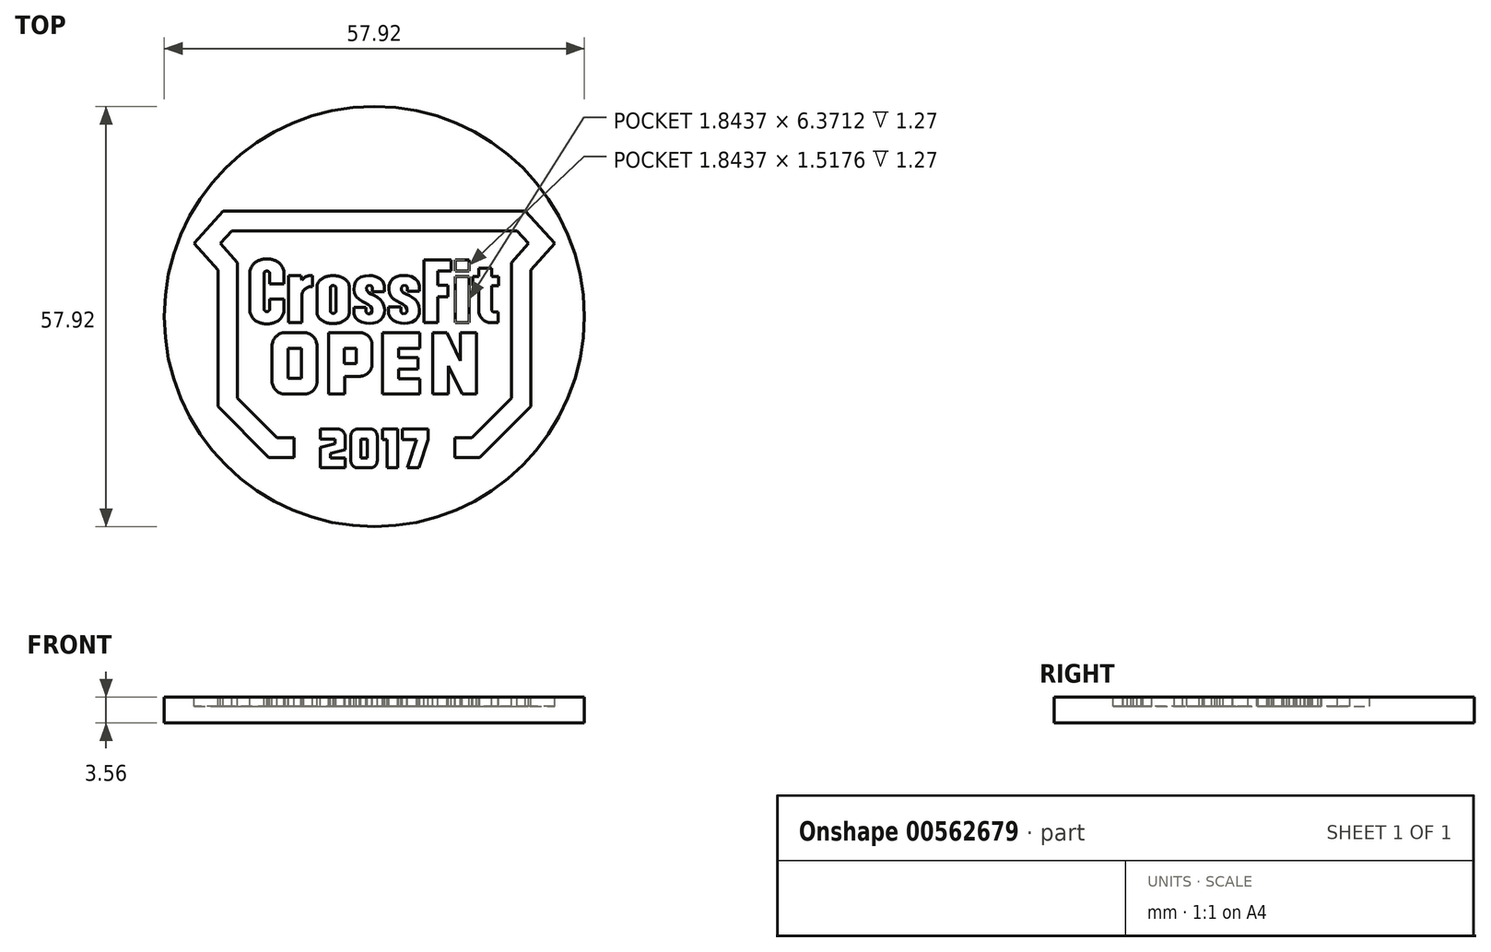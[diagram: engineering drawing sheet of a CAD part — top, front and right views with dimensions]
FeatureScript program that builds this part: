
annotation { "Feature Type Name" : "Feature", "Feature Type Description" : "" }
export const myFeature = defineFeature(function(context is Context, id is Id, definition is map)
    precondition{}
    {
        {
            var Q0;
            Q0=qCreatedBy(makeId("Top.planeOp"),FACE);
            var sketch = newSketch(context, id + "F0", { "sketchPlane" : qUnion([Q0])});
            skCircle(sketch, "E0", {"center": v(0, 0) * mm, "radius": 28.96 * mm});
            skSolve(sketch);
        }
        {
            var Q0;
            Q0=makeQuery(id+"F0.imprint","IMPRINT",FACE,{"disambiguationData":[TD([[makeQuery(id+"F0.imprint","IMPRINT",EDGE,{"derivedFrom":sQuery(id+"F0.wireOp",EDGE,"E0")}),1.0]])]});
            extrude(context, id + "F1", {"entities" : qUnion([Q0]), "depth" : 3.56 * mm, "offsetDistance" : 25.4 * mm});
        }
        {
            var Q0;
            Q0=makeQuery(id+"F1.opExtrude","CAP_FACE",FACE,{"disambiguationData":[OSD([sQuery(id+"F0.wireOp",EDGE,"E0")])],"isStart":false});
            var sketch = newSketch(context, id + "F2", { "sketchPlane" : qUnion([Q0])});
            skPoint(sketch, "E1", {"position": v(0.13, -0.67) * mm});
            skLineSegment(sketch, "E2", {"start": v(-15.2, 14.53) * mm, "end": v(-15.2, 11.82) * mm});
            skLineSegment(sketch, "E3", {"start": v(-15.2, 11.82) * mm, "end": v(-19.67, 11.82) * mm});
            skLineSegment(sketch, "E4", {"start": v(-19.67, 11.82) * mm, "end": v(-21.25, 10.06) * mm});
            skLineSegment(sketch, "E5", {"start": v(-21.25, 10.06) * mm, "end": v(-18.9, 7.43) * mm});
            skLineSegment(sketch, "E6", {"start": v(-18.9, 7.43) * mm, "end": v(-18.9, -11.25) * mm});
            skLineSegment(sketch, "E7", {"start": v(-18.9, -11.25) * mm, "end": v(-13.44, -16.74) * mm});
            skLineSegment(sketch, "E8", {"start": v(-13.44, -16.74) * mm, "end": v(-11.07, -16.74) * mm});
            skLineSegment(sketch, "E9", {"start": v(-11.07, -16.74) * mm, "end": v(-11.07, -19.45) * mm});
            skLineSegment(sketch, "E10", {"start": v(-11.07, -19.45) * mm, "end": v(-14.54, -19.45) * mm});
            skLineSegment(sketch, "E11", {"start": v(-14.54, -19.45) * mm, "end": v(-21.55, -12.4) * mm});
            skLineSegment(sketch, "E12", {"start": v(-21.55, -12.4) * mm, "end": v(-21.55, 6.37) * mm});
            skLineSegment(sketch, "E13", {"start": v(-21.55, 6.37) * mm, "end": v(-24.85, 10.06) * mm});
            skLineSegment(sketch, "E14", {"start": v(-24.85, 10.06) * mm, "end": v(-20.84, 14.53) * mm});
            skLineSegment(sketch, "E15", {"start": v(-20.84, 14.53) * mm, "end": v(-15.2, 14.53) * mm});
            skLineSegment(sketch, "E16", {"start": v(-14.42, 6) * mm, "end": v(-14.42, 4.47) * mm});
            skLineSegment(sketch, "E17", {"start": v(-14.42, 4.47) * mm, "end": v(-12.48, 4.47) * mm});
            skLineSegment(sketch, "E18", {"start": v(-12.48, 4.47) * mm, "end": v(-12.48, 6.3) * mm});
            skLineSegment(sketch, "E19", {"start": v(-17.15, 6.3) * mm, "end": v(-17.15, 0.62) * mm});
            skLineSegment(sketch, "E20", {"start": v(-14.42, 1) * mm, "end": v(-14.42, 2.43) * mm});
            skLineSegment(sketch, "E21", {"start": v(-14.42, 2.43) * mm, "end": v(-12.48, 2.43) * mm});
            skLineSegment(sketch, "E22", {"start": v(-12.48, 2.43) * mm, "end": v(-12.48, 0.62) * mm});
            skLineSegment(sketch, "E23", {"start": v(-15.2, 6) * mm, "end": v(-15.2, 1) * mm});
            skArc(sketch, "E24", {"start": v(-14.42, 6) * mm, "mid": v(-14.81, 6.27) * mm, "end": v(-15.2, 6) * mm});
            skArc(sketch, "E25", {"start": v(-15.2, 1) * mm, "mid": v(-14.81, 0.68) * mm, "end": v(-14.42, 1) * mm});
            skLineSegment(sketch, "E26", {"start": v(-9.97, 5) * mm, "end": v(-10.1, 5.63) * mm});
            skLineSegment(sketch, "E27", {"start": v(-10.1, 5.63) * mm, "end": v(-11.83, 5.63) * mm});
            skLineSegment(sketch, "E28", {"start": v(-11.83, 5.63) * mm, "end": v(-11.83, -0.85) * mm});
            skLineSegment(sketch, "E29", {"start": v(-11.83, -0.85) * mm, "end": v(-9.98, -0.85) * mm});
            skLineSegment(sketch, "E30", {"start": v(-9.98, -0.85) * mm, "end": v(-9.98, 3.1) * mm});
            skLineSegment(sketch, "E31", {"start": v(-8.5, 5.65) * mm, "end": v(-8.5, 4.11) * mm});
            skArc(sketch, "E32", {"start": v(-8.5, 5.65) * mm, "mid": v(-9.32, 5.53) * mm, "end": v(-9.97, 5) * mm});
            skArc(sketch, "E33", {"start": v(-8.5, 4.11) * mm, "mid": v(-9.44, 3.9) * mm, "end": v(-9.98, 3.1) * mm});
            skLineSegment(sketch, "E34", {"start": v(-7.89, 4.2) * mm, "end": v(-7.89, 0.46) * mm});
            skLineSegment(sketch, "E35", {"start": v(-3.47, 4.2) * mm, "end": v(-3.47, 0.46) * mm});
            skLineSegment(sketch, "E36", {"start": v(-6.05, 4.04) * mm, "end": v(-6.05, 0.68) * mm});
            skLineSegment(sketch, "E37", {"start": v(-5.3, 0.68) * mm, "end": v(-5.3, 4.04) * mm});
            skArc(sketch, "E38", {"start": v(-5.3, 4.04) * mm, "mid": v(-5.68, 4.28) * mm, "end": v(-6.05, 4.04) * mm});
            skArc(sketch, "E39", {"start": v(-6.05, 0.68) * mm, "mid": v(-5.68, 0.43) * mm, "end": v(-5.3, 0.68) * mm});
            skLineSegment(sketch, "E40", {"start": v(-5.68, 3.86) * mm, "end": v(-5.68, 0.84) * mm, "construction": true});
            skLineSegment(sketch, "E41", {"start": v(-7.89, 2.33) * mm, "end": v(-3.47, 2.33) * mm, "construction": true});
            skFitSpline(sketch, "E42.MirrorCS", {"points": [v(-3.47, 4.2) * mm, v(-3.93, 5.06) * mm, v(-4.62, 5.46) * mm, v(-5.68, 5.64) * mm], "startDerivative": vector(-0.46, 3.85) * mm, "endDerivative": vector(-4.22, 0.16) * mm});
            skFitSpline(sketch, "E43.MirrorCS", {"points": [v(-7.89, 0.46) * mm, v(-7.42, -0.4) * mm, v(-6.74, -0.8) * mm, v(-5.68, -0.98) * mm], "startDerivative": vector(0.46, -3.85) * mm, "endDerivative": vector(4.22, -0.16) * mm});
            skFitSpline(sketch, "E44.MirrorCS", {"points": [v(-3.47, 0.46) * mm, v(-3.93, -0.4) * mm, v(-4.62, -0.8) * mm, v(-5.68, -0.98) * mm], "startDerivative": vector(-0.46, -3.85) * mm, "endDerivative": vector(-4.22, -0.16) * mm});
            skFitSpline(sketch, "E45", {"points": [v(-17.15, 6.3) * mm, v(-16.64, 7.26) * mm, v(-16, 7.69) * mm, v(-14.81, 7.96) * mm], "startDerivative": vector(0.97, 4.15) * mm, "endDerivative": vector(4.22, 0.16) * mm});
            skLineSegment(sketch, "E46", {"start": v(-14.81, 5.84) * mm, "end": v(-14.81, 1.08) * mm, "construction": true});
            skFitSpline(sketch, "E47.MirrorCS", {"points": [v(-12.48, 6.3) * mm, v(-12.99, 7.26) * mm, v(-13.62, 7.69) * mm, v(-14.81, 7.96) * mm], "startDerivative": vector(-0.97, 4.15) * mm, "endDerivative": vector(-4.22, 0.16) * mm});
            skLineSegment(sketch, "E48", {"start": v(-17.15, 3.46) * mm, "end": v(-14.81, 3.46) * mm, "construction": true});
            skFitSpline(sketch, "E49.MirrorCS", {"points": [v(-17.15, 0.62) * mm, v(-16.64, -0.34) * mm, v(-16, -0.77) * mm, v(-14.81, -1.04) * mm], "startDerivative": vector(0.97, -4.15) * mm, "endDerivative": vector(4.22, -0.16) * mm});
            skFitSpline(sketch, "E50.MirrorCS", {"points": [v(-12.48, 0.62) * mm, v(-12.99, -0.34) * mm, v(-13.62, -0.77) * mm, v(-14.81, -1.04) * mm], "startDerivative": vector(-0.97, -4.15) * mm, "endDerivative": vector(-4.22, -0.16) * mm});
            skFitSpline(sketch, "E51.MirrorCS", {"points": [v(-7.89, 4.2) * mm, v(-7.42, 5.06) * mm, v(-6.74, 5.46) * mm, v(-5.68, 5.64) * mm], "startDerivative": vector(0.46, 3.85) * mm, "endDerivative": vector(4.22, 0.16) * mm});
            skLineSegment(sketch, "E52", {"start": v(-0.27, 4.07) * mm, "end": v(-0.27, 3.44) * mm});
            skLineSegment(sketch, "E53", {"start": v(-0.27, 3.44) * mm, "end": v(1.39, 3.44) * mm});
            skLineSegment(sketch, "E54", {"start": v(1.39, 3.44) * mm, "end": v(1.39, 4.25) * mm});
            skFitSpline(sketch, "E55", {"points": [v(1.39, 4.25) * mm, v(1.25, 4.73) * mm, v(0.96, 5.08) * mm, v(0.56, 5.36) * mm, v(0, 5.56) * mm, v(-0.4, 5.63) * mm, v(-0.7, 5.64) * mm, v(-1.07, 5.62) * mm, v(-1.62, 5.53) * mm, v(-2.03, 5.35) * mm, v(-2.4, 5.07) * mm, v(-2.62, 4.73) * mm, v(-2.76, 4.31) * mm, v(-2.8, 3.96) * mm, v(-2.78, 3.56) * mm, v(-2.7, 3.15) * mm, v(-2.47, 2.72) * mm, v(-2.25, 2.47) * mm, v(-1.97, 2.27) * mm, v(-1.61, 2.07) * mm, v(-1.3, 1.9) * mm, v(-1.02, 1.76) * mm, v(-0.75, 1.6) * mm, v(-0.5, 1.4) * mm, v(-0.41, 1.28) * mm, v(-0.32, 1.08) * mm, v(-0.3, 0.79) * mm, v(-0.34, 0.57) * mm, v(-0.46, 0.43) * mm, v(-0.64, 0.38) * mm, v(-0.84, 0.39) * mm, v(-1.03, 0.44) * mm, v(-1.16, 0.63) * mm], "startDerivative": vector(-2.14, 14.98) * mm, "endDerivative": vector(-3.94, 13.1) * mm});
            skLineSegment(sketch, "E56", {"start": v(-2.83, 0.39) * mm, "end": v(-2.83, 1.28) * mm});
            skLineSegment(sketch, "E57", {"start": v(-2.83, 1.28) * mm, "end": v(-1.16, 1.28) * mm});
            skLineSegment(sketch, "E58", {"start": v(-1.16, 1.28) * mm, "end": v(-1.16, 0.63) * mm});
            skFitSpline(sketch, "E59", {"points": [v(-2.83, 0.39) * mm, v(-2.67, -0.07) * mm, v(-2.35, -0.45) * mm, v(-1.98, -0.69) * mm, v(-1.5, -0.86) * mm, v(-1.03, -0.94) * mm, v(-0.7, -0.95) * mm, v(-0.34, -0.94) * mm, v(0.21, -0.84) * mm, v(0.6, -0.67) * mm, v(0.97, -0.39) * mm, v(1.22, -0.06) * mm, v(1.37, 0.3) * mm, v(1.42, 0.75) * mm, v(1.4, 1.11) * mm, v(1.3, 1.54) * mm, v(1.1, 1.95) * mm, v(0.87, 2.26) * mm, v(0.6, 2.5) * mm, v(0.3, 2.7) * mm, v(0, 2.88) * mm, v(-0.33, 3.05) * mm, v(-0.58, 3.18) * mm, v(-0.81, 3.31) * mm, v(-0.96, 3.44) * mm, v(-1.07, 3.64) * mm, v(-1.08, 3.86) * mm, v(-1.06, 4.07) * mm, v(-0.94, 4.24) * mm, v(-0.75, 4.3) * mm, v(-0.56, 4.29) * mm, v(-0.4, 4.23) * mm, v(-0.27, 4.07) * mm], "startDerivative": vector(2.14, -14.98) * mm, "endDerivative": vector(3.94, -13.1) * mm});
            skLineSegment(sketch, "E60", {"start": v(4.54, 4.08) * mm, "end": v(4.54, 3.45) * mm});
            skLineSegment(sketch, "E61", {"start": v(4.54, 3.45) * mm, "end": v(6.2, 3.45) * mm});
            skLineSegment(sketch, "E62", {"start": v(6.2, 3.45) * mm, "end": v(6.2, 4.26) * mm});
            skFitSpline(sketch, "E63", {"points": [v(6.2, 4.26) * mm, v(6.06, 4.74) * mm, v(5.77, 5.1) * mm, v(5.37, 5.37) * mm, v(4.81, 5.57) * mm, v(4.4, 5.64) * mm, v(4.11, 5.65) * mm, v(3.74, 5.63) * mm, v(3.2, 5.54) * mm, v(2.78, 5.36) * mm, v(2.42, 5.08) * mm, v(2.2, 4.74) * mm, v(2.05, 4.32) * mm, v(2.02, 3.97) * mm, v(2.03, 3.57) * mm, v(2.11, 3.16) * mm, v(2.34, 2.73) * mm, v(2.56, 2.48) * mm, v(2.84, 2.28) * mm, v(3.2, 2.08) * mm, v(3.52, 1.92) * mm, v(3.8, 1.77) * mm, v(4.06, 1.6) * mm, v(4.3, 1.41) * mm, v(4.4, 1.3) * mm, v(4.5, 1.09) * mm, v(4.5, 0.8) * mm, v(4.47, 0.58) * mm, v(4.35, 0.44) * mm, v(4.17, 0.39) * mm, v(3.97, 0.4) * mm, v(3.78, 0.45) * mm, v(3.65, 0.64) * mm], "startDerivative": vector(-2.14, 14.98) * mm, "endDerivative": vector(-3.94, 13.1) * mm});
            skLineSegment(sketch, "E64", {"start": v(1.98, 0.4) * mm, "end": v(1.98, 1.3) * mm});
            skLineSegment(sketch, "E65", {"start": v(1.98, 1.3) * mm, "end": v(3.65, 1.3) * mm});
            skLineSegment(sketch, "E66", {"start": v(3.65, 1.3) * mm, "end": v(3.65, 0.64) * mm});
            skFitSpline(sketch, "E67", {"points": [v(1.98, 0.4) * mm, v(2.14, -0.06) * mm, v(2.46, -0.44) * mm, v(2.83, -0.68) * mm, v(3.31, -0.85) * mm, v(3.78, -0.93) * mm, v(4.12, -0.95) * mm, v(4.47, -0.93) * mm, v(5.02, -0.83) * mm, v(5.42, -0.66) * mm, v(5.78, -0.38) * mm, v(6.03, -0.05) * mm, v(6.18, 0.32) * mm, v(6.23, 0.76) * mm, v(6.2, 1.12) * mm, v(6.12, 1.55) * mm, v(5.92, 1.96) * mm, v(5.68, 2.27) * mm, v(5.4, 2.5) * mm, v(5.1, 2.71) * mm, v(4.8, 2.89) * mm, v(4.48, 3.06) * mm, v(4.23, 3.2) * mm, v(4, 3.32) * mm, v(3.85, 3.45) * mm, v(3.74, 3.65) * mm, v(3.73, 3.87) * mm, v(3.75, 4.08) * mm, v(3.87, 4.25) * mm, v(4.06, 4.3) * mm, v(4.25, 4.3) * mm, v(4.42, 4.24) * mm, v(4.54, 4.08) * mm], "startDerivative": vector(2.14, -14.98) * mm, "endDerivative": vector(3.94, -13.1) * mm});
            skLineSegment(sketch, "E68", {"start": v(10.61, 7.8) * mm, "end": v(6.85, 7.8) * mm});
            skLineSegment(sketch, "E69", {"start": v(6.85, 7.8) * mm, "end": v(6.85, -0.85) * mm});
            skLineSegment(sketch, "E70", {"start": v(6.85, -0.85) * mm, "end": v(8.77, -0.85) * mm});
            skLineSegment(sketch, "E71", {"start": v(8.77, -0.85) * mm, "end": v(8.77, 2.7) * mm});
            skLineSegment(sketch, "E72", {"start": v(8.77, 2.7) * mm, "end": v(10.16, 2.7) * mm});
            skLineSegment(sketch, "E73", {"start": v(10.16, 2.7) * mm, "end": v(10.16, 4.29) * mm});
            skLineSegment(sketch, "E74", {"start": v(10.16, 4.29) * mm, "end": v(8.77, 4.29) * mm});
            skLineSegment(sketch, "E75", {"start": v(8.77, 4.29) * mm, "end": v(8.77, 6.28) * mm});
            skLineSegment(sketch, "E76", {"start": v(8.77, 6.28) * mm, "end": v(10.61, 6.28) * mm});
            skLineSegment(sketch, "E77", {"start": v(10.61, 6.28) * mm, "end": v(10.61, 7.8) * mm});
            skLineSegment(sketch, "E78", {"start": v(11.2, 7.8) * mm, "end": v(13.03, 7.8) * mm});
            skLineSegment(sketch, "E79", {"start": v(13.03, 7.8) * mm, "end": v(13.03, 6.28) * mm});
            skLineSegment(sketch, "E80", {"start": v(13.03, 6.28) * mm, "end": v(11.2, 6.28) * mm});
            skLineSegment(sketch, "E81", {"start": v(11.2, 6.28) * mm, "end": v(11.2, 7.8) * mm});
            skLineSegment(sketch, "E82", {"start": v(11.2, 5.52) * mm, "end": v(13.03, 5.52) * mm});
            skLineSegment(sketch, "E83", {"start": v(13.03, 5.52) * mm, "end": v(13.03, -0.85) * mm});
            skLineSegment(sketch, "E84", {"start": v(13.03, -0.85) * mm, "end": v(11.2, -0.85) * mm});
            skLineSegment(sketch, "E85", {"start": v(11.2, -0.85) * mm, "end": v(11.2, 5.52) * mm});
            skLineSegment(sketch, "E86", {"start": v(14.38, 6.63) * mm, "end": v(16.2, 6.63) * mm});
            skLineSegment(sketch, "E87", {"start": v(16.2, 6.63) * mm, "end": v(16.2, 5.52) * mm});
            skLineSegment(sketch, "E88", {"start": v(16.2, 5.52) * mm, "end": v(17.15, 5.52) * mm});
            skLineSegment(sketch, "E89", {"start": v(17.15, 5.52) * mm, "end": v(17.15, 4.23) * mm});
            skLineSegment(sketch, "E90", {"start": v(17.15, 4.23) * mm, "end": v(16.2, 4.23) * mm});
            skLineSegment(sketch, "E91", {"start": v(16.2, 4.23) * mm, "end": v(16.2, 0.92) * mm});
            skLineSegment(sketch, "E92", {"start": v(14.38, 6.63) * mm, "end": v(14.38, 5.52) * mm});
            skLineSegment(sketch, "E93", {"start": v(14.38, 5.52) * mm, "end": v(13.6, 5.52) * mm});
            skLineSegment(sketch, "E94", {"start": v(13.6, 5.52) * mm, "end": v(13.6, 4.23) * mm});
            skLineSegment(sketch, "E95", {"start": v(13.6, 4.23) * mm, "end": v(14.38, 4.23) * mm});
            skLineSegment(sketch, "E96", {"start": v(14.38, 4.23) * mm, "end": v(14.38, 0.85) * mm});
            skLineSegment(sketch, "E97", {"start": v(16.51, 0.61) * mm, "end": v(17.08, 0.61) * mm});
            skLineSegment(sketch, "E98", {"start": v(17.08, 0.61) * mm, "end": v(17.08, -0.85) * mm});
            skLineSegment(sketch, "E99", {"start": v(17.08, -0.85) * mm, "end": v(16.09, -0.85) * mm});
            skArc(sketch, "E100", {"start": v(14.38, 0.85) * mm, "mid": v(14.88, -0.35) * mm, "end": v(16.09, -0.85) * mm});
            skArc(sketch, "E101", {"start": v(16.2, 0.92) * mm, "mid": v(16.3, 0.7) * mm, "end": v(16.51, 0.61) * mm});
            skLineSegment(sketch, "E102", {"start": v(0, 18.62) * mm, "end": v(0, -25.74) * mm, "construction": true});
            skLineSegment(sketch, "E103.MirrorCS", {"start": v(15.2, 14.53) * mm, "end": v(15.2, 11.82) * mm});
            skLineSegment(sketch, "E104.MirrorCS", {"start": v(20.84, 14.53) * mm, "end": v(15.2, 14.53) * mm});
            skLineSegment(sketch, "E105.MirrorCS", {"start": v(24.85, 10.06) * mm, "end": v(20.84, 14.53) * mm});
            skLineSegment(sketch, "E106.MirrorCS", {"start": v(21.55, 6.37) * mm, "end": v(24.85, 10.06) * mm});
            skLineSegment(sketch, "E107.MirrorCS", {"start": v(21.55, -12.4) * mm, "end": v(21.55, 6.37) * mm});
            skLineSegment(sketch, "E108.MirrorCS", {"start": v(14.54, -19.45) * mm, "end": v(21.55, -12.4) * mm});
            skLineSegment(sketch, "E109.MirrorCS", {"start": v(11.07, -19.45) * mm, "end": v(14.54, -19.45) * mm});
            skLineSegment(sketch, "E110.MirrorCS", {"start": v(11.07, -16.74) * mm, "end": v(11.07, -19.45) * mm});
            skLineSegment(sketch, "E111.MirrorCS", {"start": v(13.44, -16.74) * mm, "end": v(11.07, -16.74) * mm});
            skLineSegment(sketch, "E112.MirrorCS", {"start": v(18.9, -11.25) * mm, "end": v(13.44, -16.74) * mm});
            skLineSegment(sketch, "E113.MirrorCS", {"start": v(18.9, 7.43) * mm, "end": v(18.9, -11.25) * mm});
            skLineSegment(sketch, "E114.MirrorCS", {"start": v(21.25, 10.06) * mm, "end": v(18.9, 7.43) * mm});
            skLineSegment(sketch, "E115.MirrorCS", {"start": v(19.67, 11.82) * mm, "end": v(21.25, 10.06) * mm});
            skLineSegment(sketch, "E116.MirrorCS", {"start": v(15.2, 11.82) * mm, "end": v(19.67, 11.82) * mm});
            skLineSegment(sketch, "E117", {"start": v(-5.1, -15.5) * mm, "end": v(-7.45, -15.5) * mm});
            skLineSegment(sketch, "E118", {"start": v(-7.45, -15.5) * mm, "end": v(-7.45, -16.87) * mm});
            skLineSegment(sketch, "E119", {"start": v(-7.45, -16.87) * mm, "end": v(-5.44, -16.87) * mm});
            skLineSegment(sketch, "E120", {"start": v(-5.44, -16.87) * mm, "end": v(-5.44, -17.52) * mm});
            skLineSegment(sketch, "E121", {"start": v(-5.44, -17.52) * mm, "end": v(-7.45, -18.02) * mm});
            skLineSegment(sketch, "E122", {"start": v(-7.45, -18.02) * mm, "end": v(-7.45, -20.86) * mm});
            skLineSegment(sketch, "E123", {"start": v(-7.45, -20.86) * mm, "end": v(-4, -20.86) * mm});
            skLineSegment(sketch, "E124", {"start": v(-4, -20.86) * mm, "end": v(-4, -19.5) * mm});
            skLineSegment(sketch, "E125", {"start": v(-4, -19.5) * mm, "end": v(-6.05, -19.5) * mm});
            skLineSegment(sketch, "E126", {"start": v(-6.05, -19.5) * mm, "end": v(-6.05, -18.84) * mm});
            skLineSegment(sketch, "E127", {"start": v(-6.05, -18.84) * mm, "end": v(-4, -18.34) * mm});
            skLineSegment(sketch, "E128", {"start": v(-4, -18.34) * mm, "end": v(-4, -16.6) * mm});
            skArc(sketch, "E129", {"start": v(-4, -16.6) * mm, "mid": v(-4.32, -15.83) * mm, "end": v(-5.1, -15.5) * mm});
            skLineSegment(sketch, "E130", {"start": v(-2.29, -15.5) * mm, "end": v(-0.56, -15.5) * mm});
            skLineSegment(sketch, "E131", {"start": v(-3.24, -16.46) * mm, "end": v(-3.24, -19.9) * mm});
            skLineSegment(sketch, "E132", {"start": v(-2.29, -20.86) * mm, "end": v(-0.56, -20.86) * mm});
            skLineSegment(sketch, "E133", {"start": v(0.4, -16.46) * mm, "end": v(0.4, -19.9) * mm});
            skArc(sketch, "E134", {"start": v(-2.29, -15.5) * mm, "mid": v(-2.96, -15.78) * mm, "end": v(-3.24, -16.46) * mm});
            skArc(sketch, "E135", {"start": v(0.4, -16.46) * mm, "mid": v(0.12, -15.78) * mm, "end": v(-0.56, -15.5) * mm});
            skArc(sketch, "E136", {"start": v(-3.24, -19.9) * mm, "mid": v(-2.96, -20.58) * mm, "end": v(-2.29, -20.86) * mm});
            skArc(sketch, "E137", {"start": v(-0.56, -20.86) * mm, "mid": v(0.12, -20.58) * mm, "end": v(0.4, -19.9) * mm});
            skLineSegment(sketch, "E138", {"start": v(1.1, -15.5) * mm, "end": v(3.22, -15.5) * mm});
            skLineSegment(sketch, "E139", {"start": v(3.22, -15.5) * mm, "end": v(3.22, -20.86) * mm});
            skLineSegment(sketch, "E140", {"start": v(3.22, -20.86) * mm, "end": v(1.77, -20.86) * mm});
            skLineSegment(sketch, "E141", {"start": v(1.77, -20.86) * mm, "end": v(1.77, -16.97) * mm});
            skLineSegment(sketch, "E142", {"start": v(1.77, -16.97) * mm, "end": v(1.1, -16.97) * mm});
            skLineSegment(sketch, "E143", {"start": v(1.1, -16.97) * mm, "end": v(1.1, -15.5) * mm});
            skLineSegment(sketch, "E144", {"start": v(3.84, -15.5) * mm, "end": v(7.43, -15.5) * mm});
            skLineSegment(sketch, "E145", {"start": v(7.43, -15.5) * mm, "end": v(7.43, -16.97) * mm});
            skLineSegment(sketch, "E146", {"start": v(7.43, -16.97) * mm, "end": v(6.14, -20.86) * mm});
            skLineSegment(sketch, "E147", {"start": v(6.14, -20.86) * mm, "end": v(4.53, -20.86) * mm});
            skLineSegment(sketch, "E148", {"start": v(4.53, -20.86) * mm, "end": v(5.83, -16.97) * mm});
            skLineSegment(sketch, "E149", {"start": v(5.83, -16.97) * mm, "end": v(3.84, -16.97) * mm});
            skLineSegment(sketch, "E150", {"start": v(3.84, -16.97) * mm, "end": v(3.84, -15.5) * mm});
            skLineSegment(sketch, "E151", {"start": v(-1.85, -16.87) * mm, "end": v(-0.99, -16.87) * mm});
            skLineSegment(sketch, "E152", {"start": v(-0.99, -16.87) * mm, "end": v(-0.99, -19.51) * mm});
            skLineSegment(sketch, "E153", {"start": v(-0.99, -19.51) * mm, "end": v(-1.85, -19.51) * mm});
            skLineSegment(sketch, "E154", {"start": v(-1.85, -19.51) * mm, "end": v(-1.85, -16.87) * mm});
            skLineSegment(sketch, "E155", {"start": v(-15.2, 14.53) * mm, "end": v(15.2, 14.53) * mm});
            skLineSegment(sketch, "E156", {"start": v(-15.2, 11.82) * mm, "end": v(15.2, 11.82) * mm});
            skLineSegment(sketch, "E157", {"start": v(-14.1, -4.04) * mm, "end": v(-14.1, -8.95) * mm});
            skLineSegment(sketch, "E158", {"start": v(-12.3, -10.7) * mm, "end": v(-9.74, -10.7) * mm});
            skLineSegment(sketch, "E159", {"start": v(-7.9, -8.95) * mm, "end": v(-7.9, -4.04) * mm});
            skLineSegment(sketch, "E160", {"start": v(-12.3, -2.22) * mm, "end": v(-9.74, -2.22) * mm});
            skArc(sketch, "E161", {"start": v(-12.3, -2.22) * mm, "mid": v(-13.57, -2.77) * mm, "end": v(-14.1, -4.04) * mm});
            skArc(sketch, "E162", {"start": v(-7.9, -4.04) * mm, "mid": v(-8.44, -2.75) * mm, "end": v(-9.74, -2.22) * mm});
            skArc(sketch, "E163", {"start": v(-9.74, -10.7) * mm, "mid": v(-8.44, -10.22) * mm, "end": v(-7.9, -8.95) * mm});
            skArc(sketch, "E164", {"start": v(-14.1, -8.95) * mm, "mid": v(-13.55, -10.19) * mm, "end": v(-12.3, -10.7) * mm});
            skLineSegment(sketch, "E165.bottom", {"start": v(-11.9, -4.38) * mm, "end": v(-10.07, -4.38) * mm});
            skLineSegment(sketch, "E165.top", {"start": v(-11.9, -8.53) * mm, "end": v(-10.07, -8.53) * mm});
            skLineSegment(sketch, "E165.left", {"start": v(-11.9, -4.38) * mm, "end": v(-11.9, -8.53) * mm});
            skLineSegment(sketch, "E165.right", {"start": v(-10.07, -4.38) * mm, "end": v(-10.07, -8.53) * mm});
            skLineSegment(sketch, "E166", {"start": v(-6.28, -2.22) * mm, "end": v(-6.28, -10.7) * mm});
            skLineSegment(sketch, "E167", {"start": v(-6.28, -10.7) * mm, "end": v(-4.11, -10.7) * mm});
            skLineSegment(sketch, "E168", {"start": v(-4.11, -10.7) * mm, "end": v(-4.11, -8.24) * mm});
            skLineSegment(sketch, "E169", {"start": v(-4.11, -8.24) * mm, "end": v(-2.07, -8.24) * mm});
            skLineSegment(sketch, "E170", {"start": v(-6.28, -2.22) * mm, "end": v(-2.07, -2.22) * mm});
            skLineSegment(sketch, "E171", {"start": v(-0.3, -3.92) * mm, "end": v(-0.3, -6.53) * mm});
            skArc(sketch, "E172", {"start": v(-0.3, -3.92) * mm, "mid": v(-0.83, -2.7) * mm, "end": v(-2.07, -2.22) * mm});
            skArc(sketch, "E173", {"start": v(-2.07, -8.24) * mm, "mid": v(-0.83, -7.76) * mm, "end": v(-0.3, -6.53) * mm});
            skLineSegment(sketch, "E174.bottom", {"start": v(-4.13, -4.4) * mm, "end": v(-2.47, -4.4) * mm});
            skLineSegment(sketch, "E174.top", {"start": v(-4.13, -6.49) * mm, "end": v(-2.47, -6.49) * mm});
            skLineSegment(sketch, "E174.left", {"start": v(-4.13, -4.4) * mm, "end": v(-4.13, -6.49) * mm});
            skLineSegment(sketch, "E174.right", {"start": v(-2.47, -4.4) * mm, "end": v(-2.47, -6.49) * mm});
            skLineSegment(sketch, "E175", {"start": v(1.15, -2.22) * mm, "end": v(1.15, -10.7) * mm});
            skLineSegment(sketch, "E176", {"start": v(1.15, -10.7) * mm, "end": v(6.3, -10.7) * mm});
            skLineSegment(sketch, "E177", {"start": v(6.3, -10.7) * mm, "end": v(6.3, -8.56) * mm});
            skLineSegment(sketch, "E178", {"start": v(6.3, -8.56) * mm, "end": v(3.35, -8.56) * mm});
            skLineSegment(sketch, "E179", {"start": v(3.35, -8.56) * mm, "end": v(3.35, -7.26) * mm});
            skLineSegment(sketch, "E180", {"start": v(3.35, -7.26) * mm, "end": v(6.04, -7.26) * mm});
            skLineSegment(sketch, "E181", {"start": v(6.04, -7.26) * mm, "end": v(6.04, -5.67) * mm});
            skLineSegment(sketch, "E182", {"start": v(6.04, -5.67) * mm, "end": v(3.35, -5.66) * mm});
            skLineSegment(sketch, "E183", {"start": v(3.35, -5.66) * mm, "end": v(3.35, -4.36) * mm});
            skLineSegment(sketch, "E184", {"start": v(3.35, -4.36) * mm, "end": v(6.3, -4.36) * mm});
            skLineSegment(sketch, "E185", {"start": v(6.3, -4.36) * mm, "end": v(6.3, -2.22) * mm});
            skLineSegment(sketch, "E186", {"start": v(6.3, -2.22) * mm, "end": v(1.15, -2.22) * mm});
            skLineSegment(sketch, "E187", {"start": v(8.05, -2.22) * mm, "end": v(8.05, -10.7) * mm});
            skLineSegment(sketch, "E188", {"start": v(8.05, -10.7) * mm, "end": v(10.24, -10.7) * mm});
            skLineSegment(sketch, "E189", {"start": v(10.24, -10.7) * mm, "end": v(10.24, -6.84) * mm});
            skLineSegment(sketch, "E190", {"start": v(10.24, -6.84) * mm, "end": v(12.13, -10.7) * mm});
            skLineSegment(sketch, "E191", {"start": v(12.13, -10.7) * mm, "end": v(14.07, -10.7) * mm});
            skLineSegment(sketch, "E192", {"start": v(14.07, -10.7) * mm, "end": v(14.07, -2.22) * mm});
            skLineSegment(sketch, "E193", {"start": v(14.07, -2.22) * mm, "end": v(11.89, -2.22) * mm});
            skLineSegment(sketch, "E194", {"start": v(11.89, -2.22) * mm, "end": v(11.89, -6.08) * mm});
            skLineSegment(sketch, "E195", {"start": v(11.89, -6.08) * mm, "end": v(10, -2.22) * mm});
            skLineSegment(sketch, "E196", {"start": v(10, -2.22) * mm, "end": v(8.05, -2.22) * mm});
            skCircle(sketch, "E197", {"center": v(0, 0) * mm, "radius": 28.9 * mm});
            skSolve(sketch);
        }
        {
            var Q0;
            Q0=makeQuery(id+"F2.imprint","IMPRINT",FACE,{"disambiguationData":[TD([[makeQuery(id+"F2.imprint","IMPRINT",EDGE,{"derivedFrom":sQuery(id+"F2.wireOp",EDGE,"E2")}),1.0]])]});
            var Q1;
            Q1=makeQuery(id+"F2.imprint","IMPRINT",FACE,{"disambiguationData":[TD([[makeQuery(id+"F2.imprint","IMPRINT",EDGE,{"derivedFrom":sQuery(id+"F2.wireOp",EDGE,"E103.MirrorCS")}),1.0]])]});
            var Q2;
            Q2=makeQuery(id+"F2.imprint","IMPRINT",FACE,{"disambiguationData":[TD([[makeQuery(id+"F2.imprint","IMPRINT",EDGE,{"derivedFrom":sQuery(id+"F2.wireOp",EDGE,"E2")}),-1.0]])]});
            var Q3;
            Q3=makeQuery(id+"F2.imprint","IMPRINT",FACE,{"disambiguationData":[TD([[makeQuery(id+"F2.imprint","IMPRINT",EDGE,{"derivedFrom":sQuery(id+"F2.wireOp",EDGE,"E16")}),1.0]])]});
            var Q4;
            Q4=makeQuery(id+"F2.imprint","IMPRINT",FACE,{"disambiguationData":[TD([[makeQuery(id+"F2.imprint","IMPRINT",EDGE,{"derivedFrom":sQuery(id+"F2.wireOp",EDGE,"E26")}),1.0]])]});
            var Q5;
            Q5=makeQuery(id+"F2.imprint","IMPRINT",FACE,{"disambiguationData":[TD([[makeQuery(id+"F2.imprint","IMPRINT",EDGE,{"derivedFrom":sQuery(id+"F2.wireOp",EDGE,"E34")}),1.0]])]});
            var Q6;
            Q6=makeQuery(id+"F2.imprint","IMPRINT",FACE,{"disambiguationData":[TD([[makeQuery(id+"F2.imprint","IMPRINT",EDGE,{"derivedFrom":sQuery(id+"F2.wireOp",EDGE,"E52")}),1.0]])]});
            var Q7;
            Q7=makeQuery(id+"F2.imprint","IMPRINT",FACE,{"disambiguationData":[TD([[makeQuery(id+"F2.imprint","IMPRINT",EDGE,{"derivedFrom":sQuery(id+"F2.wireOp",EDGE,"E60")}),1.0]])]});
            var Q8;
            Q8=makeQuery(id+"F2.imprint","IMPRINT",FACE,{"disambiguationData":[TD([[makeQuery(id+"F2.imprint","IMPRINT",EDGE,{"derivedFrom":sQuery(id+"F2.wireOp",EDGE,"E68")}),1.0]])]});
            var Q9;
            Q9=makeQuery(id+"F2.imprint","IMPRINT",FACE,{"disambiguationData":[TD([[makeQuery(id+"F2.imprint","IMPRINT",EDGE,{"derivedFrom":sQuery(id+"F2.wireOp",EDGE,"E82")}),-1.0]])]});
            var Q10;
            Q10=makeQuery(id+"F2.imprint","IMPRINT",FACE,{"disambiguationData":[TD([[makeQuery(id+"F2.imprint","IMPRINT",EDGE,{"derivedFrom":sQuery(id+"F2.wireOp",EDGE,"E78")}),-1.0]])]});
            var Q11;
            Q11=makeQuery(id+"F2.imprint","IMPRINT",FACE,{"disambiguationData":[TD([[makeQuery(id+"F2.imprint","IMPRINT",EDGE,{"derivedFrom":sQuery(id+"F2.wireOp",EDGE,"E86")}),-1.0]])]});
            var Q12;
            Q12=makeQuery(id+"F2.imprint","IMPRINT",FACE,{"disambiguationData":[TD([[makeQuery(id+"F2.imprint","IMPRINT",EDGE,{"derivedFrom":sQuery(id+"F2.wireOp",EDGE,"E187")}),1.0]])]});
            var Q13;
            Q13=makeQuery(id+"F2.imprint","IMPRINT",FACE,{"disambiguationData":[TD([[makeQuery(id+"F2.imprint","IMPRINT",EDGE,{"derivedFrom":sQuery(id+"F2.wireOp",EDGE,"E175")}),1.0]])]});
            var Q14;
            Q14=makeQuery(id+"F2.imprint","IMPRINT",FACE,{"disambiguationData":[TD([[makeQuery(id+"F2.imprint","IMPRINT",EDGE,{"derivedFrom":sQuery(id+"F2.wireOp",EDGE,"E166")}),1.0]])]});
            var Q15;
            Q15=makeQuery(id+"F2.imprint","IMPRINT",FACE,{"disambiguationData":[TD([[makeQuery(id+"F2.imprint","IMPRINT",EDGE,{"derivedFrom":sQuery(id+"F2.wireOp",EDGE,"E157")}),1.0]])]});
            var Q16;
            Q16=makeQuery(id+"F2.imprint","IMPRINT",FACE,{"disambiguationData":[TD([[makeQuery(id+"F2.imprint","IMPRINT",EDGE,{"derivedFrom":sQuery(id+"F2.wireOp",EDGE,"E117")}),1.0]])]});
            var Q17;
            Q17=makeQuery(id+"F2.imprint","IMPRINT",FACE,{"disambiguationData":[TD([[makeQuery(id+"F2.imprint","IMPRINT",EDGE,{"derivedFrom":sQuery(id+"F2.wireOp",EDGE,"E130")}),-1.0]])]});
            var Q18;
            Q18=makeQuery(id+"F2.imprint","IMPRINT",FACE,{"disambiguationData":[TD([[makeQuery(id+"F2.imprint","IMPRINT",EDGE,{"derivedFrom":sQuery(id+"F2.wireOp",EDGE,"E138")}),-1.0]])]});
            var Q19;
            Q19=makeQuery(id+"F2.imprint","IMPRINT",FACE,{"disambiguationData":[TD([[makeQuery(id+"F2.imprint","IMPRINT",EDGE,{"derivedFrom":sQuery(id+"F2.wireOp",EDGE,"E144")}),-1.0]])]});
            extrude(context, id + "F3", {"entities" : qUnion([Q0, Q1, Q2, Q3, Q4, Q5, Q6, Q7, Q8, Q9, Q10, Q11, Q12, Q13, Q14, Q15, Q16, Q17, Q18, Q19]), "operationType" : NewBodyOperationType.REMOVE, "oppositeDirection" : true, "depth" : 1.27 * mm, "offsetDistance" : 25.4 * mm});
        }
    });
